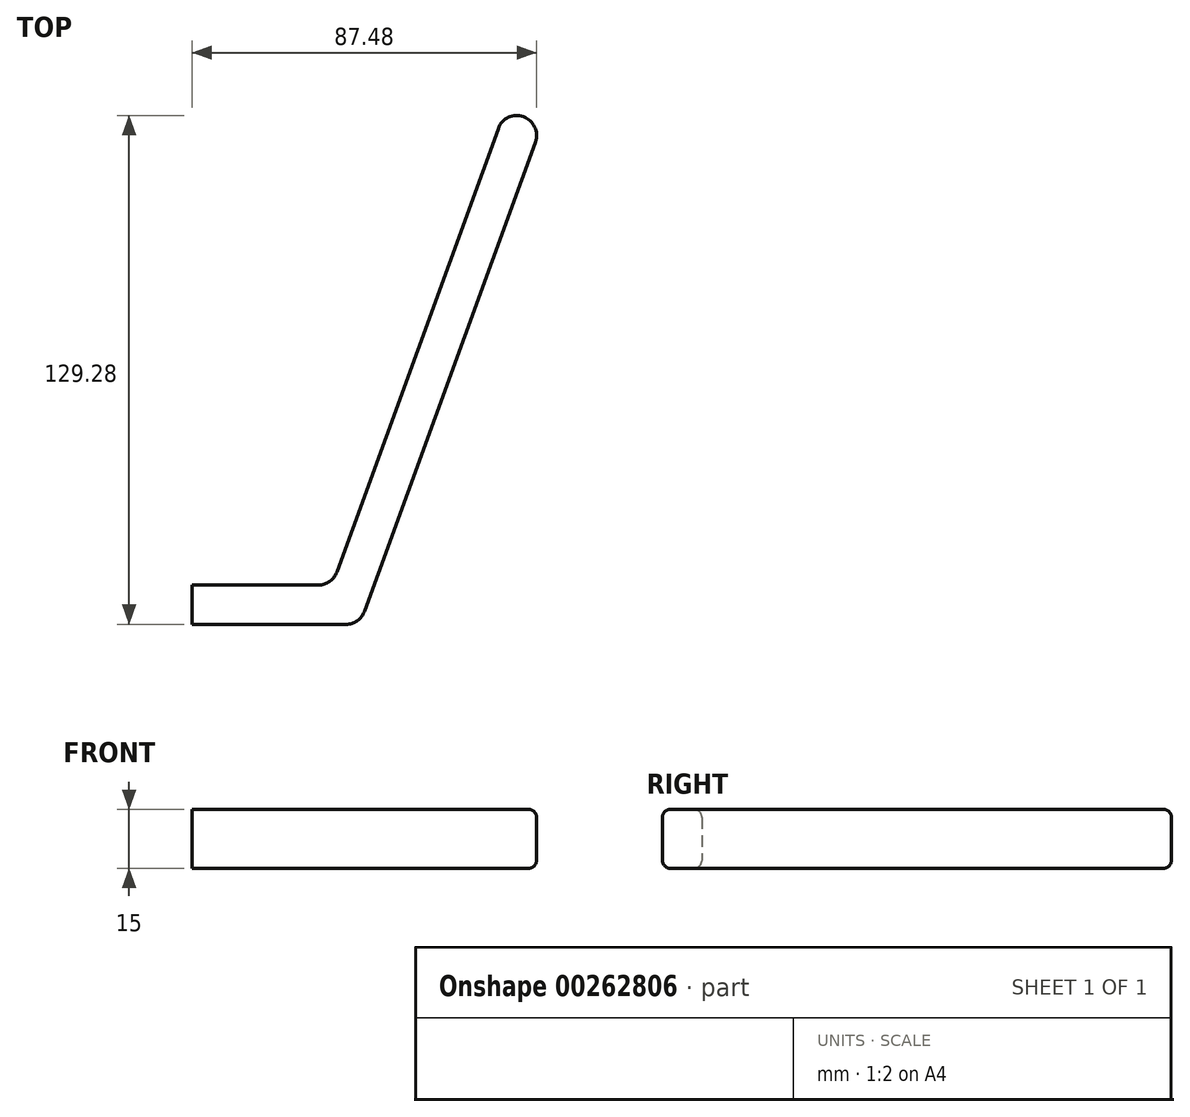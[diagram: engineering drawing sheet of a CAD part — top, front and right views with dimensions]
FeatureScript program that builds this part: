
annotation { "Feature Type Name" : "Feature", "Feature Type Description" : "" }
export const myFeature = defineFeature(function(context is Context, id is Id, definition is map)
    precondition{}
    {
        {
            var Q0;
            Q0=qCreatedBy(makeId("Top.planeOp"),FACE);
            var sketch = newSketch(context, id + "F0", { "sketchPlane" : qUnion([Q0])});
            skLineSegment(sketch, "E0", {"start": v(0, 0) * mm, "end": v(42.57, 0) * mm});
            skLineSegment(sketch, "E1", {"start": v(42.57, 0) * mm, "end": v(88.9, 127.27) * mm});
            skLineSegment(sketch, "E2", {"start": v(88.9, 127.27) * mm, "end": v(79.5, 130.7) * mm});
            skLineSegment(sketch, "E3", {"start": v(79.5, 130.7) * mm, "end": v(35.57, 10) * mm});
            skLineSegment(sketch, "E4", {"start": v(35.57, 10) * mm, "end": v(0, 10) * mm});
            skLineSegment(sketch, "E5", {"start": v(0, 10) * mm, "end": v(0, 0) * mm});
            skSolve(sketch);
        }
        {
            var Q0;
            Q0 = qSketchRegion(id + "F0", true);
            extrude(context, id + "F1", {"entities" : qUnion([Q0]), "depth" : 15 * mm});
        }
        {
            var Q0;
            Q0=makeQuery(id+"F1.opExtrude","SWEPT_EDGE",EDGE,{"disambiguationData":[OSD([sQuery(id+"F0.wireOp",EDGE,"E3"),sQuery(id+"F0.wireOp",EDGE,"E4")])]});
            var Q1;
            Q1=makeQuery(id+"F1.opExtrude","SWEPT_EDGE",EDGE,{"disambiguationData":[OSD([sQuery(id+"F0.wireOp",EDGE,"E0"),sQuery(id+"F0.wireOp",EDGE,"E1")])]});
            var Q2;
            Q2=makeQuery(id+"F1.opExtrude","SWEPT_EDGE",EDGE,{"disambiguationData":[OSD([sQuery(id+"F0.wireOp",EDGE,"E2"),sQuery(id+"F0.wireOp",EDGE,"E3")])]});
            var Q3;
            Q3=makeQuery(id+"F1.opExtrude","SWEPT_EDGE",EDGE,{"disambiguationData":[OSD([sQuery(id+"F0.wireOp",EDGE,"E1"),sQuery(id+"F0.wireOp",EDGE,"E2")])]});
            fillet(context, id + "F2", {"entities" : qUnion([Q0, Q1, Q2, Q3]), "radius" : 5 * mm, "tangentPropagation" : true, "allowEdgeOverflow" : false});
        }
        {
            var Q0;
            Q0=makeQuery(id+"F1.opExtrude","CAP_EDGE",EDGE,{"disambiguationData":[OSD([sQuery(id+"F0.wireOp",EDGE,"E3")])],"isStart":false});
            var Q1;
            Q1=makeQuery(id+"F1.opExtrude","CAP_EDGE",EDGE,{"disambiguationData":[OSD([sQuery(id+"F0.wireOp",EDGE,"E3")])],"isStart":true});
            fillet(context, id + "F3", {"entities" : qUnion([Q0, Q1]), "radius" : 2 * mm, "tangentPropagation" : true, "allowEdgeOverflow" : false});
        }
    });
